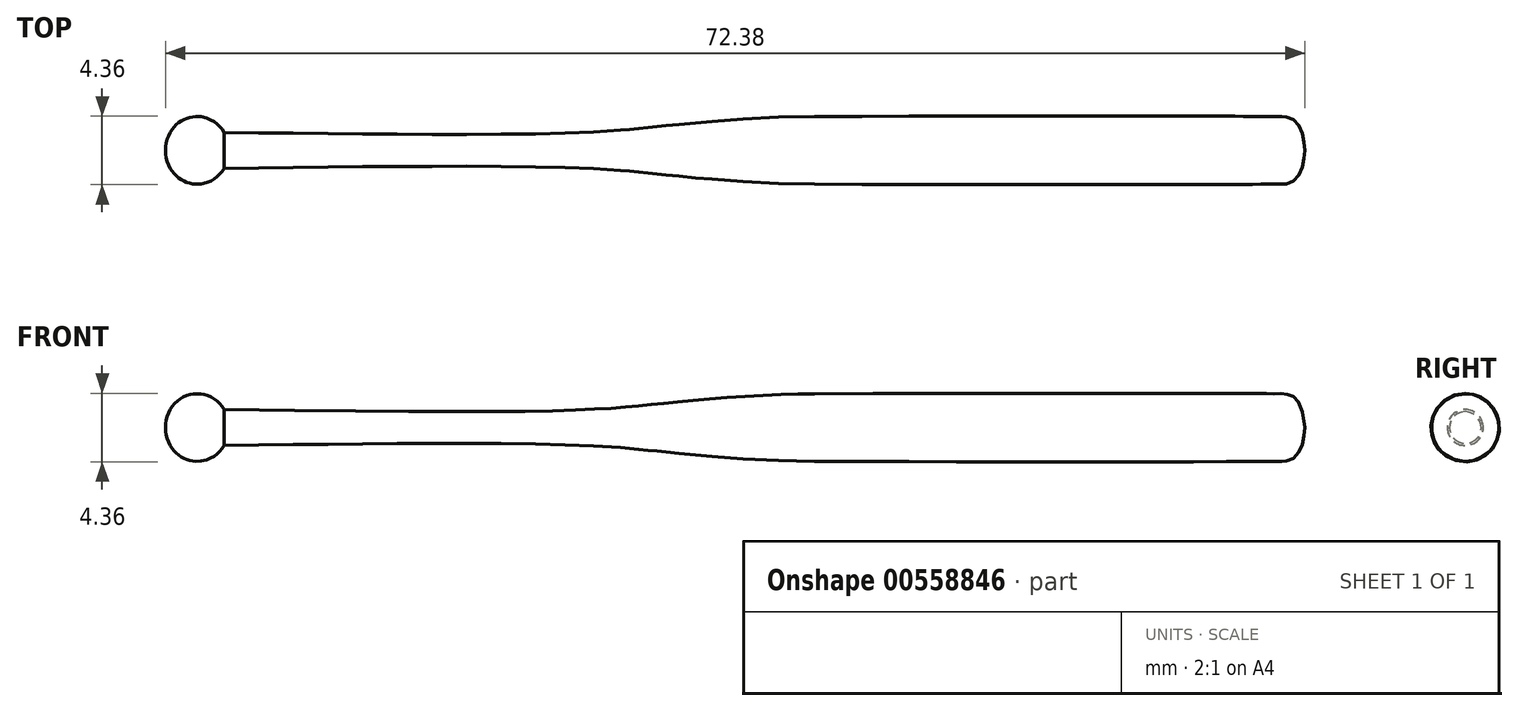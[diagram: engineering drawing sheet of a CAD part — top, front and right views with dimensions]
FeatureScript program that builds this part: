
annotation { "Feature Type Name" : "Feature", "Feature Type Description" : "" }
export const myFeature = defineFeature(function(context is Context, id is Id, definition is map)
    precondition{}
    {
        {
            var Q0;
            Q0=qCreatedBy(makeId("Front.planeOp"),FACE);
            var sketch = newSketch(context, id + "F0", { "sketchPlane" : qUnion([Q0])});
            skEllipse(sketch, "E0", {"center": v(-39.2, 0) * mm, "majorRadius": 2.15 * mm, "minorRadius": 2.01 * mm, "majorAxis": v(0, 1)});
            skPoint(sketch, "E1.0.internal.snap0", {"position": v(-39.2, 2.15) * mm});
            skPoint(sketch, "E1.2.internal.snap0", {"position": v(-39.2, 2.15) * mm});
            skFitSpline(sketch, "E1", {"points": [v(-39.2, 1.17) * mm, v(-8.87, 1.62) * mm, v(0, 2.15) * mm], "startDerivative": vector(116.73, -1.73) * mm, "endDerivative": vector(23.34, 0) * mm});
            skFitSpline(sketch, "E2.MirrorCS", {"points": [v(-39.2, -1.17) * mm, v(-8.87, -1.62) * mm, v(0, -2.15) * mm], "startDerivative": vector(116.73, 1.73) * mm, "endDerivative": vector(23.34, 0) * mm});
            skFitSpline(sketch, "E3", {"points": [v(0, 2.15) * mm, v(29.48, 2.15) * mm, v(31.16, 0) * mm], "startDerivative": vector(90, 0.23) * mm, "endDerivative": vector(2.74, -27.64) * mm});
            skFitSpline(sketch, "E4.MirrorCS", {"points": [v(0, -2.15) * mm, v(29.48, -2.15) * mm, v(31.16, 0) * mm], "startDerivative": vector(90, -0.23) * mm, "endDerivative": vector(2.74, 27.64) * mm});
            skLineSegment(sketch, "E5", {"start": v(-41.22, 0) * mm, "end": v(31.16, 0) * mm});
            skSolve(sketch);
        }
        {
            var Q0;
            {var subQ5=sQuery(id+"F0.wireOp",EDGE,"E3");Q0=makeQuery(id+"F0.imprint","IMPRINT",FACE,{"disambiguationData":[TD([[makeQuery(id+"F0.imprint","IMPRINT",EDGE,{"derivedFrom":subQ5}),-1.0]])]});}
            var Q1;
            Q1=sQuery(id+"F0.wireOp",EDGE,"E5");
            revolve(context, id + "F1", {"entities" : qUnion([Q0]), "axis" : qUnion([Q1]), "revolveType" : RevolveType.FULL});
        }
        {
            var Q0;
            {var subQ0=sQuery(id+"F0.wireOp",EDGE,"E0");var subQ1=makeQuery(id+"F0.imprint","INTERSECT",VERTEX,{"derivedFrom":[subQ0,sQuery(id+"F0.wireOp",EDGE,"E1")]});Q0=makeQuery(id+"F0.imprint","IMPRINT",FACE,{"disambiguationData":[TD([[makeQuery(id+"F0.imprint","IMPRINT",EDGE,{"disambiguationData":[TD([[subQ1,1.0]])],"derivedFrom":subQ0}),1.0]])]});}
            var Q1;
            Q1=sQuery(id+"F0.wireOp",EDGE,"E5");
            revolve(context, id + "F2", {"operationType" : NewBodyOperationType.ADD, "entities" : qUnion([Q0]), "axis" : qUnion([Q1]), "revolveType" : RevolveType.FULL});
        }
    });
